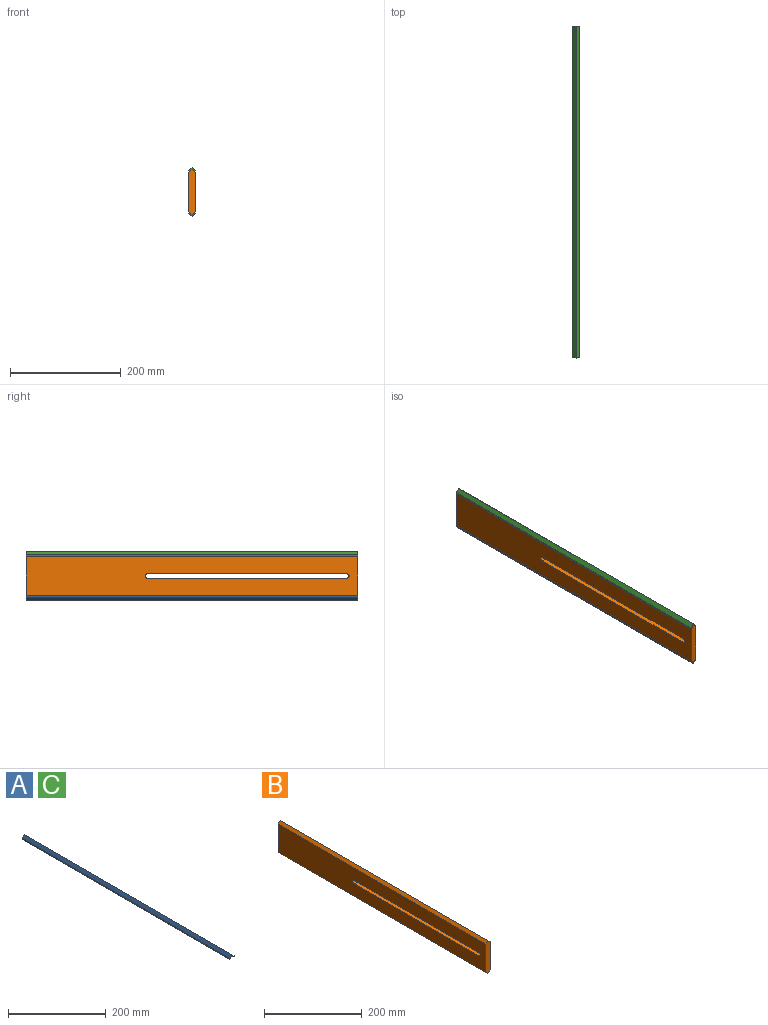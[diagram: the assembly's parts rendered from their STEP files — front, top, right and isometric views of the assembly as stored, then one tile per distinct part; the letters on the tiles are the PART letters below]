
ASSEMBLY  parts=3 mates=1
PART A: 8 faces, bbox 12x600x8.8 mm
  f0: plane 12x8.83mm, normal (0,-1,0), area 33.9mm2, adj f1,f2,f3,f5,f6,f7
  f1: plane 600x6mm, normal (-0.71,0,0.71), area 5091.2mm2, adj f0,f2,f4,f5
  f2: plane 600x6mm, normal (0.71,0,0.71), area 5091.2mm2, adj f0,f1,f3,f4
  f3: plane 600x2.83mm, normal (1,0,0), area 1697.1mm2, adj f0,f2,f4,f6
  f4: plane 12x8.83mm, normal (0,1,0), area 33.9mm2, adj f1,f2,f3,f5,f6,f7
  f5: plane 600x2.83mm, normal (-1,0,0), area 1697.1mm2, adj f0,f1,f4,f7
  f6: plane 600x6mm, normal (-0.71,0,-0.71), area 5091.2mm2, adj f0,f3,f4,f7
  f7: plane 600x6mm, normal (0.71,0,-0.71), area 5091.2mm2, adj f0,f4,f5,f6
PART B: 12 faces, bbox 12x600x82.3 mm
  f0: plane 600x70.34mm, normal (1,0,0), area 39275.6mm2, adj f3,f4,f6,f7,f8,f9,f10,f11
  f1: plane 600x70.34mm, normal (-1,0,0), area 39275.6mm2, adj f2,f5,f6,f7,f8,f9,f10,f11
  f2: plane 600x6mm, normal (-0.71,0,0.71), area 5091.2mm2, adj f1,f3,f6,f7
  f3: plane 600x6mm, normal (0.71,0,0.71), area 5091.2mm2, adj f0,f2,f6,f7
  f4: plane 600x6mm, normal (0.71,0,-0.71), area 5091.2mm2, adj f0,f5,f6,f7
  f5: plane 600x6mm, normal (-0.71,0,-0.71), area 5091.2mm2, adj f1,f4,f6,f7
  f6: plane 82.34x12mm, normal (0,-1,0), area 916.1mm2, adj f0,f1,f2,f3,f4,f5
  f7: plane 82.34x12mm, normal (0,1,0), area 916.1mm2, adj f0,f1,f2,f3,f4,f5
  f8: cylinder r=4mm len=12mm, axis (1,0,0), area 150.8mm2, adj f0,f1,f9,f11
  f9: plane 360x12mm, normal (0,0,-1), area 4320mm2, adj f0,f1,f8,f10
  f10: cylinder r=4mm len=12mm, axis (1,0,0), area 150.8mm2, adj f0,f1,f9,f11
  f11: plane 360x12mm, normal (0,0,1), area 4320mm2, adj f0,f1,f8,f10
PART C: same geometry as A
PLACE A rot(axis=(0,1,0),180deg) t=(-18,300,75)mm
PLACE B t=(6,300,-75)mm fixed
PLACE C t=(6,300,-75)mm
MATE fastened B.f6 <-> A.f0  axis (0,1,0) through (0,-300,-35.17)mm
